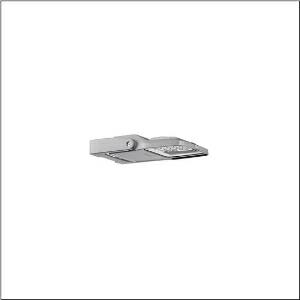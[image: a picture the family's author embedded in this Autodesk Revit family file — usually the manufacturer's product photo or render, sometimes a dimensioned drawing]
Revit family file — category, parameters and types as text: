
# Revit family: floodlight_fl_21_micro___pl52_5xa7761a2d2a_2c4a
name_source: partatom
category: Lighting Fixtures
units: mm (PartAtom-declared; Revit-internal decimal feet)

## family parameters
Cut with Voids When Loaded = No
Host = Face
Light Source = No
Part Type = Normal
Room Calculation Point = No
Round Connector Dimension = Use Diameter
Shared = No

## types (1)
- --- (1 x LED, 2890 lm, 23.1 W, 3000K)
    Apparent Load = 23 VA
    CIE Flux Codes = 26 60 98 100 100
    Color Rendering = 70
    Color Temperature = 3000K
    Default Elevation = 1800 mm
    Description = Floodlight FL 21 micro, floodlight, primary light control with lens, of PMMA, primary optical cover: protective disc, of toughened safety glass, transparent, light distribution: PL52, light emission: direct distribution, installation type: surface-mounted, LED, High Power LED, rated luminous flux: 2.890lm, luminous efficacy: 125lm/W, light colour: 730, colour temperature: 3000K, control gear: ECG iQ, control: optimised constant luminous flux control (CLO 2.0), Desk-Remote (wireless, voltage-free reading and setting of iQ features in the workshop via application-optimized NFC function/RFID function), Light-Fading, Smart-Wire, Night-Set, Lumen-Switch, Temp-Guard, Auto-Match, with terminal, 6-pole, mains connection: 220..240V, AC, 50/60Hz, start of lifetime: 23W, end of lifetime: 24W, reduction: 11W, luminaire housing, of diecast aluminium, powder-coated, Siteco® metallic grey (DB 702S), corrosivity category C5 according to DIN EN ISO 12944, design bracket, of diecast aluminium, powder-coated, Siteco® metallic grey (DB 702S), protection rating (complete): IP66, insulation class (complete): insulation class II (safety insulation), certification: CE, protection symbol: D, impact resistance: IK07, permissible operating ambient temperature: -40..+40°C, permissible operating ambient temperature for outdoor applications: -40..+50°C, standard: DIN EN 12944, packaging unit: 1 piece

Light Distribution: PL52
    Height = 65 mm
    Lamp = 1 x LED
    Lamp Light Flux = 2890 lm
    Lamp Power = 23.1 W
    Lamp count = 1
    Length = 312 mm
    Luminous efficacy = 125 lm/W
    Manufacturer = Siteco
    ModVariant = No
    Model = 5XA7761A2D2A
    Number of Poles = 1
    OnlyDefault = Yes
    Power Factor = 1
    Product Name = Floodlight FL 21 micro | PL52
    Product group = floodlight | pylon top
    ProductGroupID = 6101
    Protection Class = Protection class II
    Protection Degree = IP 66
    RLX_Detail_Level = 1
    RlxData = <blob elided: 97325 chars, md5=0094c0e4>
    Socket = socket
    Standby Power = 0 W
    System Light Flux = 2890 lm
    System Power = 23 W
    Type Comments = factory setting: luminous flux: 100 % | dim-lin: 254 | 455 mA
    Type Image = l_1006878.jpg
    URL = http://relux.com
    VarID = @adj_090829
    Voltage = 0 V
    Weight = 0.00 kg
    Width = 230 mm

## geometry (parser evidence)
native form markers: Blend x4, Sweep x13
no freeform markers — native parametric forms only
